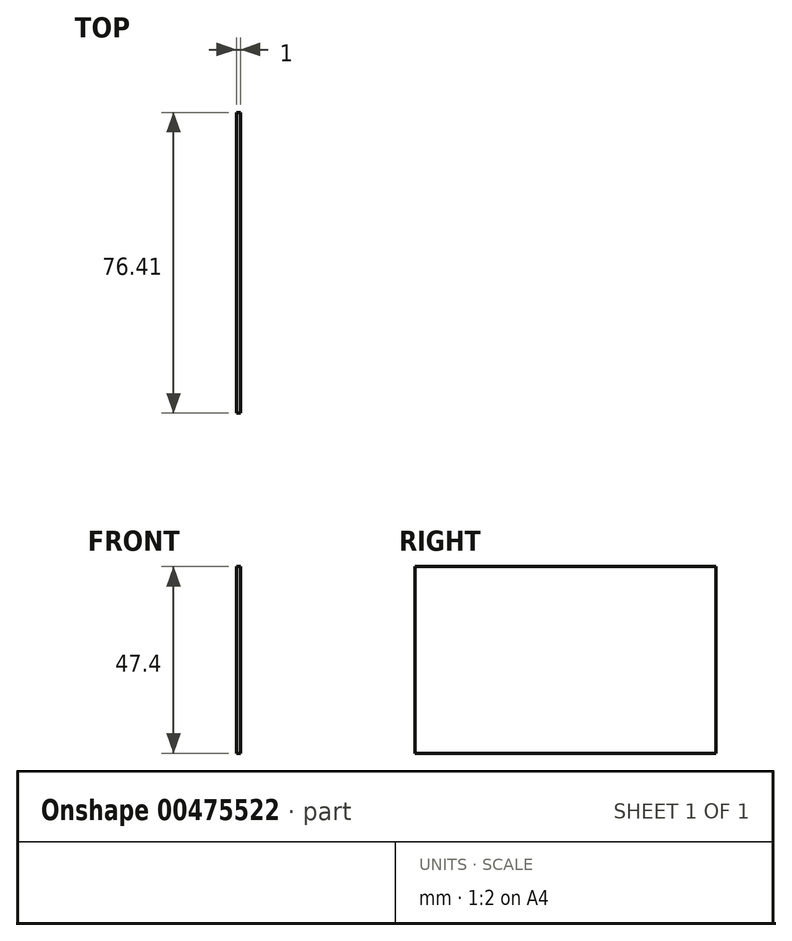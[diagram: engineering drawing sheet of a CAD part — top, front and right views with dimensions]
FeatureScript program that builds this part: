
annotation { "Feature Type Name" : "Feature", "Feature Type Description" : "" }
export const myFeature = defineFeature(function(context is Context, id is Id, definition is map)
    precondition{}
    {
        {
            var Q0;
            Q0=qCreatedBy(makeId("Right.planeOp"),FACE);
            var sketch = newSketch(context, id + "F0", { "sketchPlane" : qUnion([Q0])});
            skLineSegment(sketch, "E0.bottom", {"start": v(0, 0) * mm, "end": v(-76.4, 0) * mm});
            skLineSegment(sketch, "E0.top", {"start": v(0, 47.4) * mm, "end": v(-76.4, 47.4) * mm});
            skLineSegment(sketch, "E0.left", {"start": v(0, 0) * mm, "end": v(0, 47.4) * mm});
            skLineSegment(sketch, "E0.right", {"start": v(-76.4, 0) * mm, "end": v(-76.4, 47.4) * mm});
            skSolve(sketch);
        }
        {
            var Q0;
            Q0=makeQuery(id+"F0.imprint","IMPRINT",FACE,{"disambiguationData":[TD([[makeQuery(id+"F0.imprint","IMPRINT",EDGE,{"derivedFrom":sQuery(id+"F0.wireOp",EDGE,"E0.bottom")}),-1.0]])]});
            extrude(context, id + "F1", {"entities" : qUnion([Q0]), "depth" : 1 * mm});
        }
    });
